# Revit family: SKG1012_revit
name_source: partatom
category: Mechanical Equipment
revit_build: Autodesk Revit 2014 (Build: 20130215_1615(x64)
units: mm (PartAtom-declared; Revit-internal decimal feet)

## types (1)
- Standard
    Connector_10_Diameter = 0' - 0"
    Connector_11_Diameter = 0' - 0"
    Connector_14_Diameter = 0' - 0"
    Connector_15_Diameter = 0' - 0"
    Connector_16_Diameter = 0' - 0"
    Connector_1_Height = 0' - 0"
    Connector_1_Width = 0' - 0"
    Connector_2_Diameter = 0' - 0"
    Connector_3_Diameter = 0' - 0"
    Connector_6_Diameter = 0' - 0"
    Connector_7_Diameter = 0' - 0"
    Connector_8_Diameter = 0' - 0"
    Connector_9_Diameter = 0' - 0"
    Description = Gas Fired Humidifier
    Design Status = 1
    Manufacturer = Neptronic
    Model = SKG3110, SKG3155, SKG3180, SKG3210
    Part Number = SKG1012_revit
    URL = www.neptronic.com
    d148 = 0' - 0 1/2"
    d150 = 0' - 0 1/2"
    d152 = 0' - 0 1/2"
    d154 = 0' - 0 1/2"
    d156 = 0' - 0 1/2"
    d158 = 0' - 0 1/2"
    d160 = 0' - 0 1/2"
    d162 = 0' - 5"
    d164 = 0' - 5 1/4"
    d166 = 3' - 8 15/16"
    d168 = 3' - 9 3/16"
    d170 = 0' - 2 1/32"
    d172 = 0' - 0 1/2"
    d174 = 0' - 2 1/32"
    d176 = 0' - 2 1/32"
    d178 = 0' - 2 1/32"
    d180 = 0' - 1 9/16"
    d182 = 0' - 0 1/2"
    d184 = 0' - 0 1/2"
    d186 = 0' - 0 1/2"
    d188 = 0' - 0 1/2"
    d190 = 0' - 0 1/2"
    d192 = 0' - 0 1/2"
    d194 = 0' - 0 1/2"
    d196 = 4' - 4"
    d199 = 0' - 0"

## geometry (parser evidence)
native form markers: Sweep x1
no freeform markers — native parametric forms only
